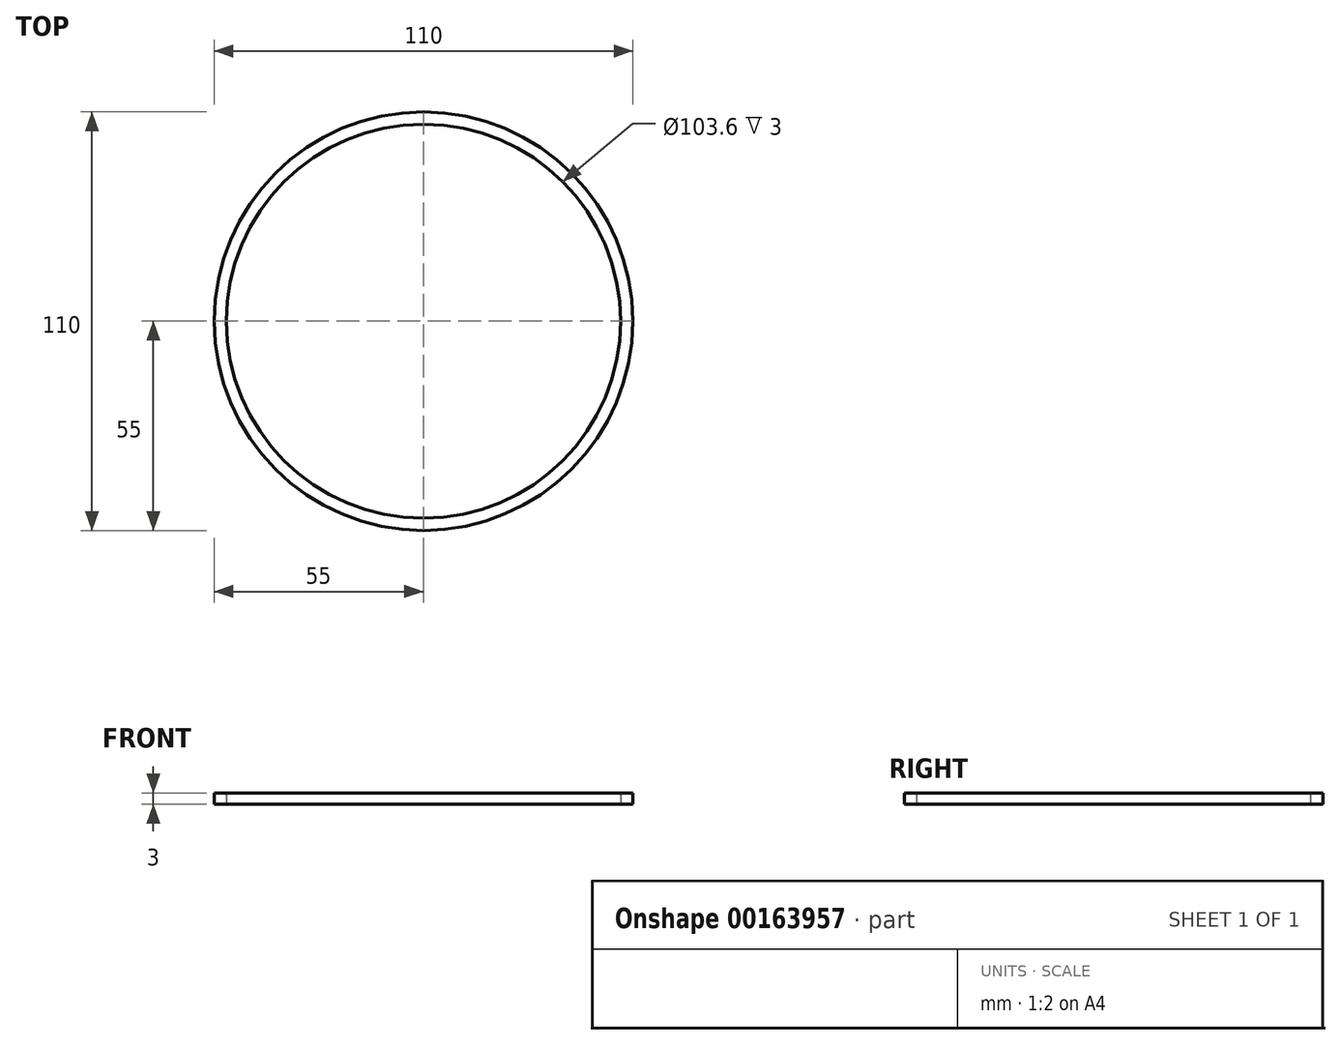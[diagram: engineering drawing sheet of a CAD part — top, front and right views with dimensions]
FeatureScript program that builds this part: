
annotation { "Feature Type Name" : "Feature", "Feature Type Description" : "" }
export const myFeature = defineFeature(function(context is Context, id is Id, definition is map)
    precondition{}
    {
        {
            var Q0;
            Q0=qCreatedBy(makeId("Top.planeOp"),FACE);
            var sketch = newSketch(context, id + "F0", { "sketchPlane" : qUnion([Q0])});
            skArc(sketch, "E0", {"start": v(-51.97, -18) * mm, "mid": v(55, 0) * mm, "end": v(-51.97, 18) * mm, "construction": true});
            skCircle(sketch, "E1", {"center": v(0, 0) * mm, "radius": 55 * mm});
            skArc(sketch, "E2", {"start": v(-51.8, 0) * mm, "mid": v(-50.99, 9.14) * mm, "end": v(-48.57, 18) * mm});
            skArc(sketch, "E3", {"start": v(-51.8, 0) * mm, "mid": v(-50.99, -9.14) * mm, "end": v(-48.57, -18) * mm});
            skArc(sketch, "E4.MirrorCS", {"start": v(51.8, 0) * mm, "mid": v(50.99, -9.14) * mm, "end": v(48.57, -18) * mm});
            skArc(sketch, "E5.MirrorCS", {"start": v(51.8, 0) * mm, "mid": v(50.99, 9.14) * mm, "end": v(48.57, 18) * mm});
            skCircle(sketch, "E6", {"center": v(0, 0) * mm, "radius": 51.8 * mm});
            skSolve(sketch);
        }
        {
            var Q0;
            Q0=qSketchRegion(id+"F0",true);
            extrude(context, id + "F1", {"entities" : qUnion([Q0]), "endBound" : BoundingType.SYMMETRIC, "depth" : 3 * mm});
        }
    });
